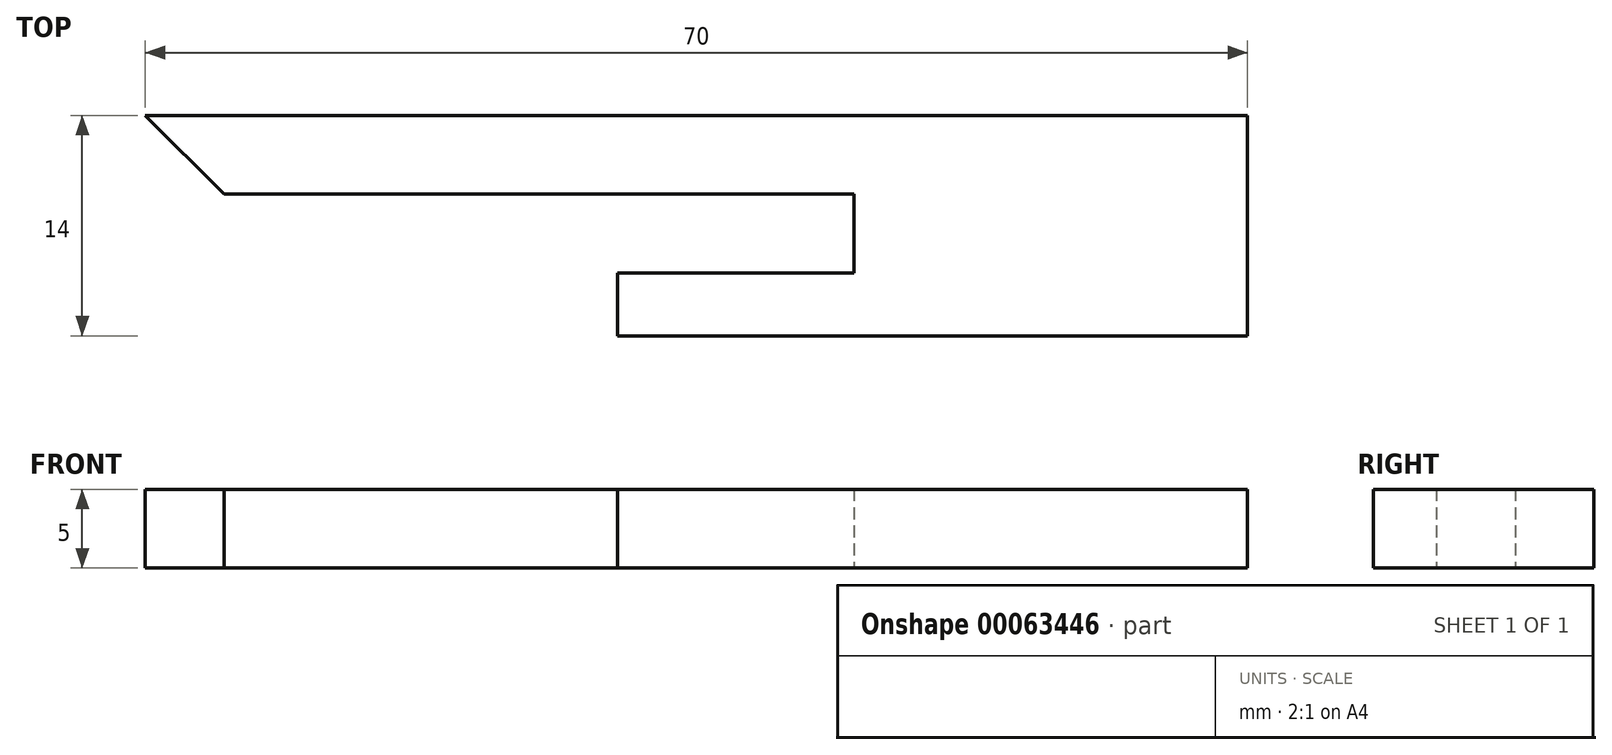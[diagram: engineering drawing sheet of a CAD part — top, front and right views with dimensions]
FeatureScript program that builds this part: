
annotation { "Feature Type Name" : "Feature", "Feature Type Description" : "" }
export const myFeature = defineFeature(function(context is Context, id is Id, definition is map)
    precondition{}
    {
        {
            var Q0;
            Q0=qCreatedBy(makeId("Top.planeOp"),FACE);
            var sketch = newSketch(context, id + "F0", { "sketchPlane" : qUnion([Q0])});
            skLineSegment(sketch, "E0.bottom", {"start": v(65, 0) * mm, "end": v(25, 0) * mm});
            skLineSegment(sketch, "E0.top", {"start": v(65, 14) * mm, "end": v(25, 14) * mm});
            skLineSegment(sketch, "E0.left", {"start": v(65, 0) * mm, "end": v(65, 14) * mm});
            skLineSegment(sketch, "E0.right", {"start": v(25, 0) * mm, "end": v(25, 4) * mm});
            skLineSegment(sketch, "E1", {"start": v(25, 9) * mm, "end": v(0, 9) * mm});
            skLineSegment(sketch, "E2", {"start": v(25, 14) * mm, "end": v(-5, 14) * mm});
            skLineSegment(sketch, "E3", {"start": v(-5, 14) * mm, "end": v(0, 9) * mm});
            skLineSegment(sketch, "E4.bottom", {"start": v(25, 9) * mm, "end": v(40, 9) * mm});
            skLineSegment(sketch, "E4.top", {"start": v(25, 4) * mm, "end": v(40, 4) * mm});
            skLineSegment(sketch, "E4.right", {"start": v(40, 9) * mm, "end": v(40, 4) * mm});
            skSolve(sketch);
        }
        {
            var Q0;
            Q0 = qSketchRegion(id + "F0", true);
            extrude(context, id + "F1", {"entities" : qUnion([Q0]), "depth" : 5 * mm});
        }
    });
